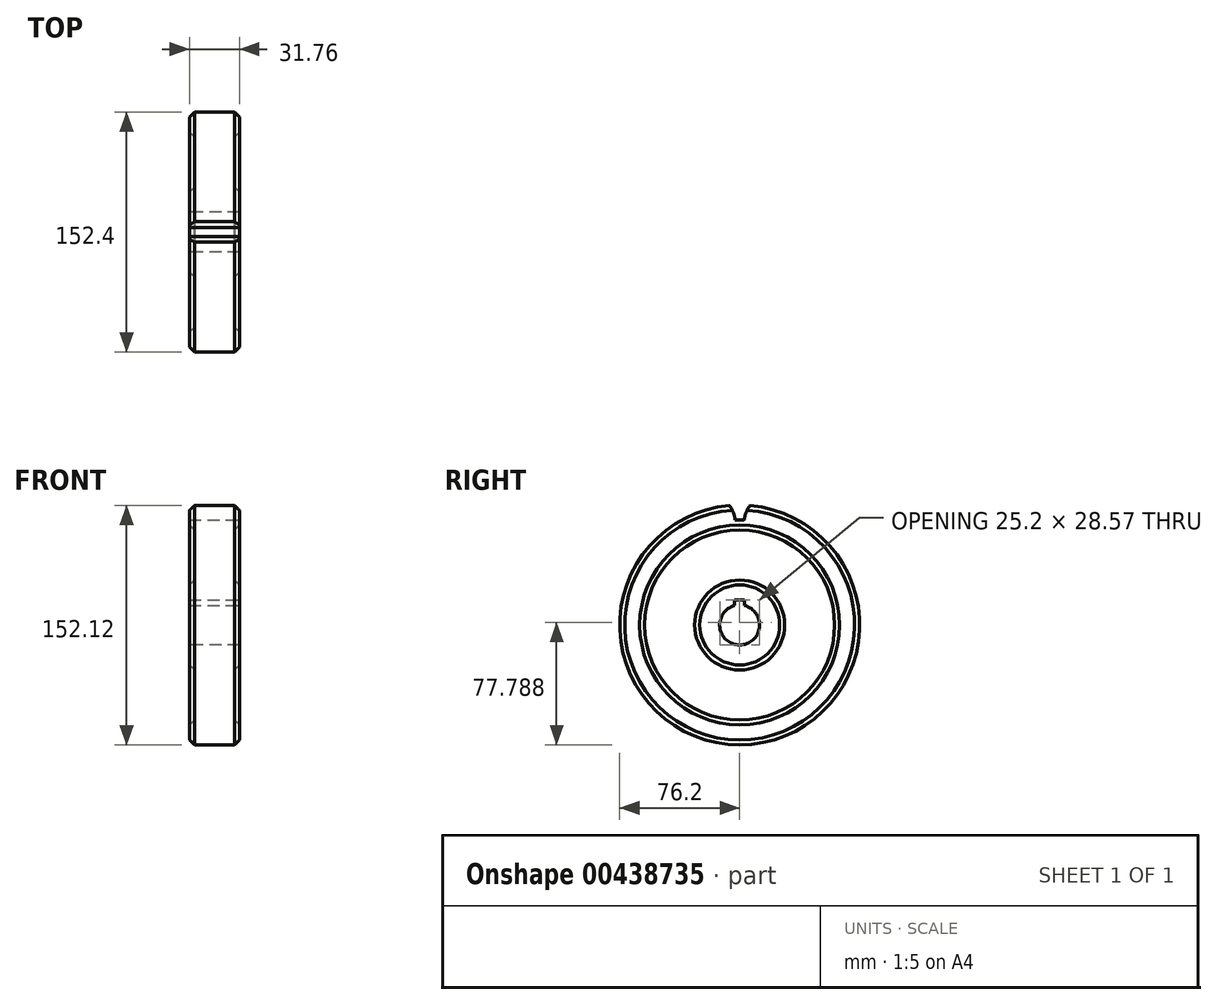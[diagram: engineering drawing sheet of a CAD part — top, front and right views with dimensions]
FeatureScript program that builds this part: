
annotation { "Feature Type Name" : "Feature", "Feature Type Description" : "" }
export const myFeature = defineFeature(function(context is Context, id is Id, definition is map)
    precondition{}
    {
        {
            var Q0;
            Q0=qCreatedBy(makeId("Front.planeOp"),FACE);
            var sketch = newSketch(context, id + "F0", { "sketchPlane" : qUnion([Q0])});
            skLineSegment(sketch, "E0", {"start": v(0, 40.66) * mm, "end": v(0, -22.84) * mm});
            skLineSegment(sketch, "E1", {"start": v(0, 40.66) * mm, "end": v(12.7, 40.66) * mm});
            skLineSegment(sketch, "E2", {"start": v(12.7, 40.66) * mm, "end": v(15.88, 37.49) * mm});
            skLineSegment(sketch, "E3", {"start": v(15.88, 37.49) * mm, "end": v(15.88, 27.96) * mm});
            skLineSegment(sketch, "E4", {"start": v(15.88, 27.96) * mm, "end": v(12.7, 24.79) * mm});
            skLineSegment(sketch, "E5", {"start": v(12.7, 24.79) * mm, "end": v(12.7, -6.96) * mm});
            skLineSegment(sketch, "E6", {"start": v(12.7, -6.96) * mm, "end": v(15.88, -10.14) * mm});
            skLineSegment(sketch, "E7", {"start": v(15.88, -10.14) * mm, "end": v(15.88, -22.84) * mm});
            skLineSegment(sketch, "E8", {"start": v(15.87, -22.84) * mm, "end": v(0, -22.84) * mm});
            skLineSegment(sketch, "E9", {"start": v(0, -22.84) * mm, "end": v(0, -35.54) * mm});
            skLineSegment(sketch, "E10", {"start": v(0, -35.54) * mm, "end": v(18.93, -35.54) * mm});
            skLineSegment(sketch, "E11.MirrorCS", {"start": v(0, 40.66) * mm, "end": v(-12.7, 40.66) * mm});
            skLineSegment(sketch, "E12.MirrorCS", {"start": v(-12.7, 40.66) * mm, "end": v(-15.88, 37.49) * mm});
            skLineSegment(sketch, "E13.MirrorCS", {"start": v(-15.88, 37.49) * mm, "end": v(-15.88, 27.96) * mm});
            skLineSegment(sketch, "E14.MirrorCS", {"start": v(-15.88, 27.96) * mm, "end": v(-12.7, 24.79) * mm});
            skLineSegment(sketch, "E15.MirrorCS", {"start": v(-12.7, 24.79) * mm, "end": v(-12.7, -6.96) * mm});
            skLineSegment(sketch, "E16.MirrorCS", {"start": v(-12.7, -6.96) * mm, "end": v(-15.87, -10.14) * mm});
            skLineSegment(sketch, "E17.MirrorCS", {"start": v(-15.88, -10.14) * mm, "end": v(-15.88, -22.84) * mm});
            skLineSegment(sketch, "E18.MirrorCS", {"start": v(-15.88, -22.84) * mm, "end": v(0, -22.84) * mm});
            skSolve(sketch);
        }
        {
            var Q0;
            Q0=makeQuery(id+"F0.imprint","IMPRINT",FACE,{"disambiguationData":[TD([[makeQuery(id+"F0.imprint","IMPRINT",EDGE,{"derivedFrom":sQuery(id+"F0.wireOp",EDGE,"E0")}),1.0]])]});
            var Q1;
            Q1=makeQuery(id+"F0.imprint","IMPRINT",FACE,{"disambiguationData":[TD([[makeQuery(id+"F0.imprint","IMPRINT",EDGE,{"derivedFrom":sQuery(id+"F0.wireOp",EDGE,"E0")}),-1.0]])]});
            var Q2;
            Q2=sQuery(id+"F0.wireOp",EDGE,"E10");
            revolve(context, id + "F1", {"entities" : qUnion([Q0, Q1]), "axis" : qUnion([Q2]), "revolveType" : RevolveType.FULL});
        }
        {
            var Q0;
            Q0=makeQuery(id+"F1.opRevolve","SWEPT_FACE",FACE,{"disambiguationData":[OSD([sQuery(id+"F0.wireOp",EDGE,"E3")])]});
            var sketch = newSketch(context, id + "F2", { "sketchPlane" : qUnion([Q0])});
            skLineSegment(sketch, "E19", {"start": v(0, -35.54) * mm, "end": v(0, 165.83) * mm});
            skLineSegment(sketch, "E20", {"start": v(0, 31.14) * mm, "end": v(2.86, 31.14) * mm});
            skArc(sketch, "E21", {"start": v(6.54, 40.38) * mm, "mid": v(4.08, 36) * mm, "end": v(2.86, 31.14) * mm});
            skLineSegment(sketch, "E22.MirrorCS", {"start": v(0, 31.14) * mm, "end": v(-2.86, 31.14) * mm});
            skArc(sketch, "E23.MirrorCS", {"start": v(-6.54, 40.38) * mm, "mid": v(-4.08, 36) * mm, "end": v(-2.86, 31.14) * mm});
            skArc(sketch, "E24.0", {"start": v(6.54, 40.38) * mm, "mid": v(0, 40.66) * mm, "end": v(-6.54, 40.38) * mm});
            skSolve(sketch);
        }
        {
            var Q0;
            {var subQ0=sQuery(id+"F2.wireOp",EDGE,"E24.0");var subQ5=sQuery(id+"F2.wireOp",EDGE,"E23.MirrorCS");var subQ6=makeQuery(id+"F2.imprint","INTERSECT",VERTEX,{"derivedFrom":[subQ5,subQ0]});Q0=makeQuery(id+"F2.imprint","IMPRINT",FACE,{"disambiguationData":[TD([[makeQuery(id+"F2.imprint","IMPRINT",EDGE,{"disambiguationData":[TD([[subQ6,1.0]])],"derivedFrom":subQ0}),1.0]])]});}
            var Q1;
            {var subQ0=sQuery(id+"F2.wireOp",EDGE,"E22.MirrorCS");Q1=makeQuery(id+"F2.imprint","IMPRINT",FACE,{"disambiguationData":[TD([[makeQuery(id+"F2.imprint","IMPRINT",EDGE,{"derivedFrom":subQ0}),-1.0]])]});}
            var Q2;
            {var subQ0=sQuery(id+"F2.wireOp",EDGE,"E20");Q2=makeQuery(id+"F2.imprint","IMPRINT",FACE,{"disambiguationData":[TD([[makeQuery(id+"F2.imprint","IMPRINT",EDGE,{"derivedFrom":subQ0}),1.0]])]});}
            var Q3;
            {var subQ0=sQuery(id+"F2.wireOp",EDGE,"E24.0");var subQ5=sQuery(id+"F2.wireOp",EDGE,"E21");var subQ6=makeQuery(id+"F2.imprint","INTERSECT",VERTEX,{"derivedFrom":[subQ5,subQ0]});Q3=makeQuery(id+"F2.imprint","IMPRINT",FACE,{"disambiguationData":[TD([[makeQuery(id+"F2.imprint","IMPRINT",EDGE,{"disambiguationData":[TD([[subQ6,-1.0]])],"derivedFrom":subQ0}),1.0]])]});}
            extrude(context, id + "F3", {"entities" : qUnion([Q0, Q1, Q2, Q3]), "operationType" : NewBodyOperationType.REMOVE, "endBound" : BoundingType.THROUGH_ALL, "oppositeDirection" : true, "depth" : 25.4 * mm});
        }
        {
            var Q0;
            Q0=makeQuery(id+"F1.opRevolve","SWEPT_FACE",FACE,{"disambiguationData":[OSD([sQuery(id+"F0.wireOp",EDGE,"E7")])]});
            var sketch = newSketch(context, id + "F4", { "sketchPlane" : qUnion([Q0])});
            skLineSegment(sketch, "E25", {"start": v(0, -35.54) * mm, "end": v(0, 67.4) * mm});
            skLineSegment(sketch, "E26", {"start": v(0, -19.66) * mm, "end": v(3.18, -19.66) * mm});
            skLineSegment(sketch, "E27", {"start": v(3.17, -19.66) * mm, "end": v(3.18, -23.24) * mm});
            skLineSegment(sketch, "E28.MirrorCS", {"start": v(0, -19.66) * mm, "end": v(-3.18, -19.66) * mm});
            skLineSegment(sketch, "E29.MirrorCS", {"start": v(-3.17, -19.66) * mm, "end": v(-3.17, -23.24) * mm});
            skArc(sketch, "E30.0", {"start": v(3.17, -23.24) * mm, "mid": v(0, -22.84) * mm, "end": v(-3.17, -23.24) * mm});
            skSolve(sketch);
        }
        {
            var Q0;
            {var subQ0=sQuery(id+"F4.wireOp",EDGE,"E28.MirrorCS");Q0=makeQuery(id+"F4.imprint","IMPRINT",FACE,{"disambiguationData":[TD([[makeQuery(id+"F4.imprint","IMPRINT",EDGE,{"derivedFrom":subQ0}),1.0]])]});}
            var Q1;
            {var subQ0=sQuery(id+"F4.wireOp",EDGE,"E26");Q1=makeQuery(id+"F4.imprint","IMPRINT",FACE,{"disambiguationData":[TD([[makeQuery(id+"F4.imprint","IMPRINT",EDGE,{"derivedFrom":subQ0}),-1.0]])]});}
            extrude(context, id + "F5", {"entities" : qUnion([Q0, Q1]), "operationType" : NewBodyOperationType.REMOVE, "endBound" : BoundingType.THROUGH_ALL, "oppositeDirection" : true, "depth" : 25.4 * mm});
        }
    });
